# Revit family: DAL_A3-Garage-4-Panel-vertical-(UK)
name_source: partatom
category: Doors
revit_build: Autodesk Revit 2016 (Build: 20150220_1215(x64)
units: mm (PartAtom-declared; Revit-internal decimal feet)

## family parameters
Always vertical = Yes
Cut with Voids When Loaded = No
Host = Wall
Room Calculation Point = No
Shared = No

## types (2) — shared parameters
Cavity Closer Depth = 85 mm  [stored 0.278871 ft]
Cavity Closer Offset from Ext = 102.5 mm  [stored 0.336286 ft]
Cavity Closer Width = 50 mm  [stored 0.164042 ft]
Door Panel Thickness = 44 mm  [stored 0.144357 ft]
FrameDepth = 89 mm  [stored 0.291995 ft]
FrameOffset - External = 25 mm  [stored 0.082021 ft]
FrameWidth = 42 mm  [stored 0.137795 ft]
Function = Interior
Handle Z Distance = 900 mm  [stored 2.95276 ft]
Material Door = Door - Panel
Material Frame = Door -  Frame/Mullion
Material Ironmongery = Door - Handle
O/A Frame Width = 64 mm  [stored 0.209974 ft]
Operation = UserDefined
Rough Width = 2271 mm  [stored 7.45079 ft]
Stile Bottom Rail = 125 mm  [stored 0.410105 ft]
Stile Hanging = 125 mm  [stored 0.410105 ft]
Stile Intermediate/Frieze = 70 mm  [stored 0.229659 ft]
Stile Top Rail = 125 mm  [stored 0.410105 ft]
Structural Tolerance = 6.5 mm
Thickness = 44 mm  [stored 0.144357 ft]
Tolerance = 3 mm  [stored 0.00984252 ft]
Undercut = 10 mm  [stored 0.0328084 ft]
Vis - Cavity Closers = Yes
Vis - Ironmongery = Yes
Wall Closure = By host
Width = 2271 mm  [stored 7.45079 ft]
Wrap Layers (Ext) from Ext = 102.5 mm  [stored 0.336286 ft]
Wrap Layers (Int) from Ext = 177.5 mm

## per-type parameters (varying)
| type | Height | Rough Height | Stile Muntin Rail |
| 2271 x 2052mm | 2052 mm  [stored 6.73228 ft] | 2052 mm  [stored 6.73228 ft] | 75 mm |
| 2271 x 2205mm Garage Door | 2205 mm  [stored 7.23425 ft] | 2205 mm  [stored 7.23425 ft] | 70 mm  [stored 0.229659 ft] |

note: [stored X ft] marks values corroborated as IEEE doubles in the binary element streams (Revit-internal decimal feet)

## geometry (parser evidence)
native form markers: Sweep x3
no freeform markers — native parametric forms only
